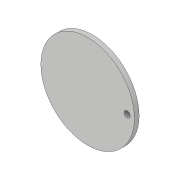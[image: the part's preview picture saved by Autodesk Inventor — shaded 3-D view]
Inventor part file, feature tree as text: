
AUTODESK INVENTOR PART (.ipt)
format: ipt  version: 2019 (Build 230136000, 136)  size: 81,920 bytes
history: native  units: in
note: dims shown in document units (in); Inventor stores cm internally (conversion verified against a paired STEP export)
features: extrude x2, sketch x2
ambient origin geometry x8: Origin, YZ Plane, XZ Plane, XY Plane, X Axis, Y Axis, Z Axis, Center Point
bodies: Solid1 (feature_tree)
feature tree (4):
  extrude  "Extrusion1"  Depth=0.0787in TaperAngle=0.0deg
  extrude  "Extrusion2"  Depth=0.0787in
  sketch  "Sketch1"  dims[d0=1.5748in d1=0.0787in d2=0.0in]
  sketch  "Sketch2"  dims[d3=0.1181in d4=0.1024in d5=0.0787in d6=0.0in]
